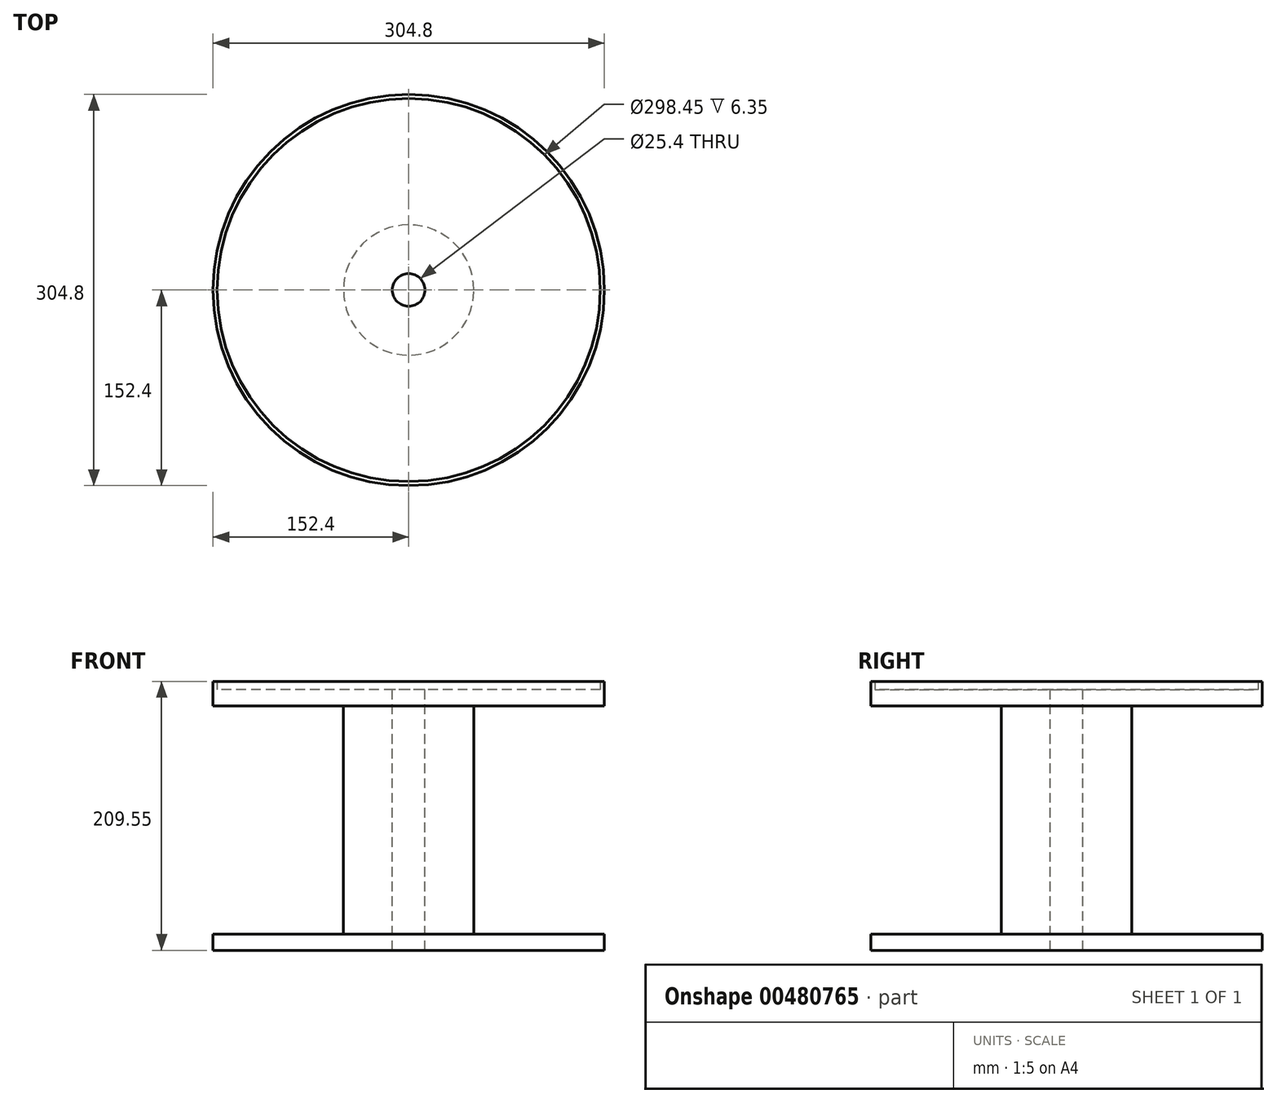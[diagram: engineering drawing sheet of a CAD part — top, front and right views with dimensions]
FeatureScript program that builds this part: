
annotation { "Feature Type Name" : "Feature", "Feature Type Description" : "" }
export const myFeature = defineFeature(function(context is Context, id is Id, definition is map)
    precondition{}
    {
        {
            var Q0;
            Q0=qCreatedBy(makeId("Top.planeOp"),FACE);
            var sketch = newSketch(context, id + "F0", { "sketchPlane" : qUnion([Q0])});
            skCircle(sketch, "E0", {"center": v(0, 0) * mm, "radius": 152.4 * mm});
            skSolve(sketch);
        }
        {
            var Q0;
            Q0=makeQuery(id+"F0.imprint","IMPRINT",FACE,{"disambiguationData":[TD([[makeQuery(id+"F0.imprint","IMPRINT",EDGE,{"derivedFrom":sQuery(id+"F0.wireOp",EDGE,"E0")}),1.0]])]});
            extrude(context, id + "F1", {"entities" : qUnion([Q0]), "depth" : 12.7 * mm, "offsetDistance" : 25.4 * mm});
        }
        {
            var Q0;
            Q0=makeQuery(id+"F1.opExtrude","CAP_FACE",FACE,{"disambiguationData":[OSD([sQuery(id+"F0.wireOp",EDGE,"E0")])],"isStart":false});
            var sketch = newSketch(context, id + "F2", { "sketchPlane" : qUnion([Q0])});
            skCircle(sketch, "E1", {"center": v(0, 0) * mm, "radius": 50.8 * mm});
            skSolve(sketch);
        }
        {
            var Q0;
            Q0=makeQuery(id+"F2.imprint","IMPRINT",FACE,{"disambiguationData":[TD([[makeQuery(id+"F2.imprint","IMPRINT",EDGE,{"derivedFrom":sQuery(id+"F2.wireOp",EDGE,"E1")}),1.0]])]});
            extrude(context, id + "F3", {"entities" : qUnion([Q0]), "operationType" : NewBodyOperationType.ADD, "depth" : 177.8 * mm, "offsetDistance" : 25.4 * mm});
        }
        {
            var Q0;
            Q0=makeQuery(id+"F3.opExtrude","CAP_FACE",FACE,{"disambiguationData":[OSD([sQuery(id+"F2.wireOp",EDGE,"E1")])],"isStart":false});
            var sketch = newSketch(context, id + "F4", { "sketchPlane" : qUnion([Q0])});
            skCircle(sketch, "E2", {"center": v(0, 0) * mm, "radius": 152.4 * mm});
            skSolve(sketch);
        }
        {
            var Q0;
            Q0=makeQuery(id+"F4.imprint","IMPRINT",FACE,{"disambiguationData":[TD([[makeQuery(id+"F4.imprint","IMPRINT",EDGE,{"derivedFrom":sQuery(id+"F4.wireOp",EDGE,"E2")}),1.0]])]});
            var Q1;
            Q1=makeQuery(id+"F4.imprint","IMPRINT",FACE,{"disambiguationData":[TD([[makeQuery(id+"F4.imprint","IMPRINT",EDGE,{"derivedFrom":makeQuery(id+"F3.opExtrude","CAP_EDGE",EDGE,{"disambiguationData":[OSD([sQuery(id+"F2.wireOp",EDGE,"E1")])],"isStart":false})}),1.0]])]});
            extrude(context, id + "F5", {"entities" : qUnion([Q0, Q1]), "operationType" : NewBodyOperationType.ADD, "depth" : 12.7 * mm, "offsetDistance" : 25.4 * mm});
        }
        {
            var Q0;
            Q0=makeQuery(id+"F5.opExtrude","CAP_FACE",FACE,{"disambiguationData":[OSD([sQuery(id+"F4.wireOp",EDGE,"E2")])],"isStart":false});
            var sketch = newSketch(context, id + "F6", { "sketchPlane" : qUnion([Q0])});
            skCircle(sketch, "E3", {"center": v(0, 0) * mm, "radius": 149.23 * mm});
            skSolve(sketch);
        }
        {
            var Q0;
            Q0=makeQuery(id+"F6.imprint","IMPRINT",FACE,{"disambiguationData":[TD([[makeQuery(id+"F6.imprint","IMPRINT",EDGE,{"derivedFrom":sQuery(id+"F6.wireOp",EDGE,"E3")}),-1.0]])]});
            extrude(context, id + "F7", {"entities" : qUnion([Q0]), "operationType" : NewBodyOperationType.ADD, "depth" : 6.35 * mm, "offsetDistance" : 25.4 * mm});
        }
        {
            var Q0;
            Q0=makeQuery(id+"F5.opExtrude","CAP_FACE",FACE,{"disambiguationData":[OSD([sQuery(id+"F4.wireOp",EDGE,"E2")])],"isStart":false});
            var sketch = newSketch(context, id + "F8", { "sketchPlane" : qUnion([Q0])});
            skCircle(sketch, "E4", {"center": v(0, 0) * mm, "radius": 12.7 * mm});
            skSolve(sketch);
        }
        {
            var Q0;
            Q0=makeQuery(id+"F8.imprint","IMPRINT",FACE,{"disambiguationData":[TD([[makeQuery(id+"F8.imprint","IMPRINT",EDGE,{"derivedFrom":sQuery(id+"F8.wireOp",EDGE,"E4")}),1.0]])]});
            extrude(context, id + "F9", {"entities" : qUnion([Q0]), "operationType" : NewBodyOperationType.REMOVE, "oppositeDirection" : true, "depth" : 457.2 * mm, "offsetDistance" : 25.4 * mm});
        }
    });
